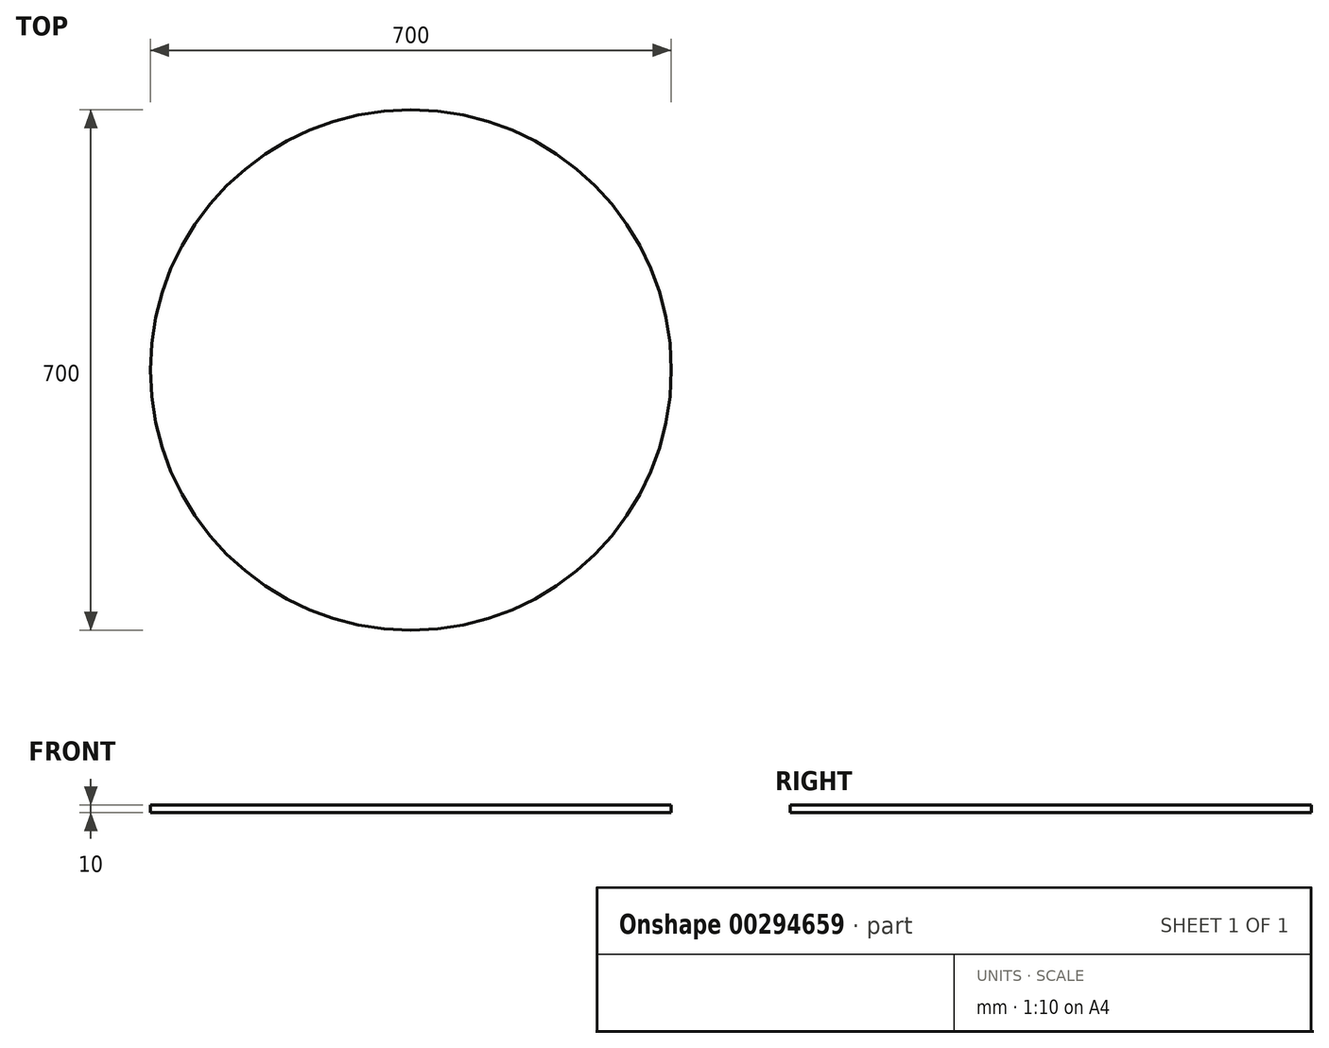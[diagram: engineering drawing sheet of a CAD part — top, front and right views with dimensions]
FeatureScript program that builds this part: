
annotation { "Feature Type Name" : "Feature", "Feature Type Description" : "" }
export const myFeature = defineFeature(function(context is Context, id is Id, definition is map)
    precondition{}
    {
        {
            var Q0;
            Q0=qCreatedBy(makeId("Top.planeOp"),FACE);
            var sketch = newSketch(context, id + "F0", { "sketchPlane" : qUnion([Q0])});
            skCircle(sketch, "E0", {"center": v(0, 0) * mm, "radius": 350 * mm});
            skSolve(sketch);
        }
        {
            var Q0;
            Q0 = qSketchRegion(id + "F0", true);
            extrude(context, id + "F1", {"entities" : qUnion([Q0]), "depth" : 10 * mm});
        }
    });
